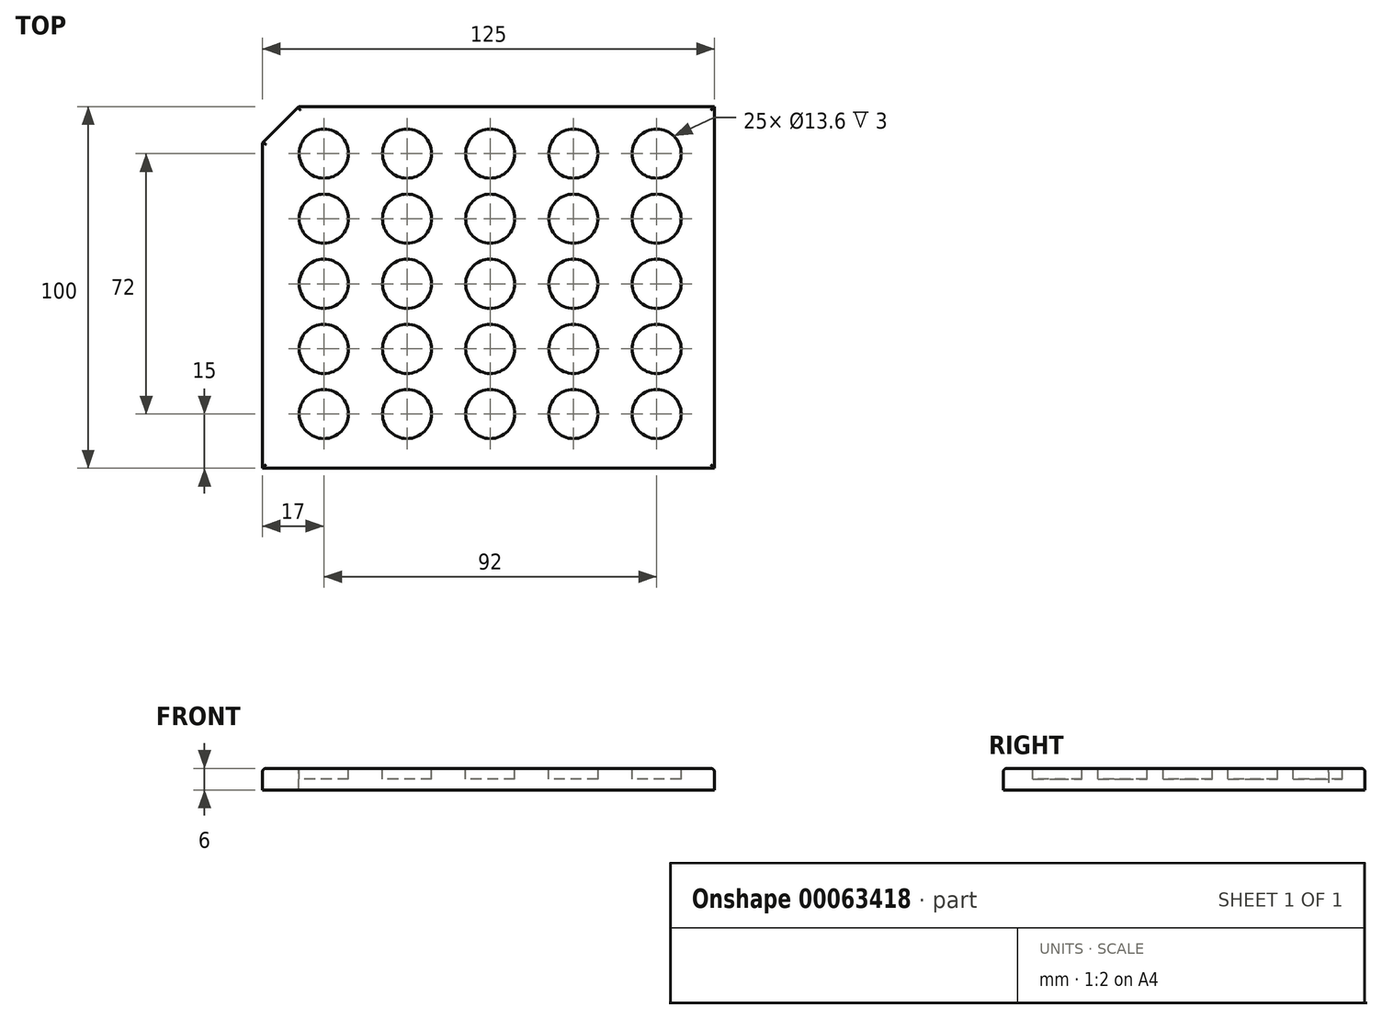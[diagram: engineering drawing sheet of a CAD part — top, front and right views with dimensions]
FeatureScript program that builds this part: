
annotation { "Feature Type Name" : "Feature", "Feature Type Description" : "" }
export const myFeature = defineFeature(function(context is Context, id is Id, definition is map)
    precondition{}
    {
        {
            var Q0;
            Q0=qCreatedBy(makeId("Top.planeOp"),FACE);
            var sketch = newSketch(context, id + "F0", { "sketchPlane" : qUnion([Q0])});
            skLineSegment(sketch, "E0.rect.bottom", {"start": v(62.5, -50) * mm, "end": v(-62.5, -50) * mm});
            skLineSegment(sketch, "E0.rect.top", {"start": v(62.5, 50) * mm, "end": v(-62.5, 50) * mm});
            skLineSegment(sketch, "E0.rect.left", {"start": v(62.5, -50) * mm, "end": v(62.5, 50) * mm});
            skLineSegment(sketch, "E0.rect.right", {"start": v(-62.5, -50) * mm, "end": v(-62.5, 50) * mm});
            skPoint(sketch, "E0.rect.middle", {"position": v(0, 0) * mm});
            skSolve(sketch);
        }
        {
            var Q0;
            Q0=qSketchRegion(id+"F0",true);
            extrude(context, id + "F1", {"entities" : qUnion([Q0]), "depth" : 6 * mm});
        }
        {
            var Q0;
            Q0=makeQuery(id+"F1.opExtrude","SWEPT_EDGE",EDGE,{"disambiguationData":[OSD([sQuery(id+"F0.wireOp",EDGE,"E0.rect.top"),sQuery(id+"F0.wireOp",EDGE,"E0.rect.right")])]});
            chamfer(context, id + "F2", {"entities" : qUnion([Q0]), "width" : 10 * mm, "tangentPropagation" : true});
        }
        {
            var Q0;
            Q0=makeQuery(id+"F1.opExtrude","CAP_EDGE",EDGE,{"disambiguationData":[OSD([sQuery(id+"F0.wireOp",EDGE,"E0.rect.right")])],"isStart":false});
            var Q1;
            Q1=makeQuery(id+"F1.opExtrude","CAP_EDGE",EDGE,{"disambiguationData":[OSD([sQuery(id+"F0.wireOp",EDGE,"E0.rect.bottom")])],"isStart":false});
            var Q2;
            Q2=makeQuery(id+"F1.opExtrude","CAP_EDGE",EDGE,{"disambiguationData":[OSD([sQuery(id+"F0.wireOp",EDGE,"E0.rect.left")])],"isStart":false});
            var Q3;
            Q3=makeQuery(id+"F1.opExtrude","CAP_EDGE",EDGE,{"disambiguationData":[OSD([sQuery(id+"F0.wireOp",EDGE,"E0.rect.top")])],"isStart":false});
            var Q4;
            {var subQ0=sQuery(id+"F0.wireOp",EDGE,"E0.rect.right");var subQ1=sQuery(id+"F0.wireOp",EDGE,"E0.rect.top");Q4=makeQuery(id+"F2.opChamfer","BLEND_EDGE",EDGE,{"blendedFrom":[makeQuery(id+"F1.opExtrude","SWEPT_EDGE",EDGE,{"disambiguationData":[OSD([subQ1,subQ0])]}),makeQuery(id+"F1.opExtrude","CAP_FACE",FACE,{"disambiguationData":[OSD([sQuery(id+"F0.wireOp",EDGE,"E0.rect.bottom"),subQ1,sQuery(id+"F0.wireOp",EDGE,"E0.rect.left"),subQ0])],"isStart":false})],"blendedInto":[makeQuery(id+"F1.opExtrude","CAP_FACE",FACE,{"disambiguationData":[OSD([sQuery(id+"F0.wireOp",EDGE,"E0.rect.bottom"),subQ1,sQuery(id+"F0.wireOp",EDGE,"E0.rect.left"),subQ0])],"isStart":false})]});}
            fillet(context, id + "F3", {"entities" : qUnion([Q0, Q1, Q2, Q3, Q4]), "radius" : 1 * mm, "tangentPropagation" : true, "allowEdgeOverflow" : false});
        }
        {
            var Q0;
            Q0=makeQuery(id+"F1.opExtrude","CAP_FACE",FACE,{"disambiguationData":[OSD([sQuery(id+"F0.wireOp",EDGE,"E0.rect.bottom"),sQuery(id+"F0.wireOp",EDGE,"E0.rect.top"),sQuery(id+"F0.wireOp",EDGE,"E0.rect.left"),sQuery(id+"F0.wireOp",EDGE,"E0.rect.right")])],"isStart":false});
            var sketch = newSketch(context, id + "F4", { "sketchPlane" : qUnion([Q0])});
            skCircle(sketch, "E1", {"center": v(46.5, 37) * mm, "radius": 6.8 * mm});
            skCircle(sketch, "E2.0.1.0", {"center": v(46.5, 19) * mm, "radius": 6.8 * mm});
            skCircle(sketch, "E2.1.0.0", {"center": v(23.5, 37) * mm, "radius": 6.8 * mm});
            skCircle(sketch, "E2.1.1.0", {"center": v(23.5, 19) * mm, "radius": 6.8 * mm});
            skCircle(sketch, "E2.2.0.0", {"center": v(0.5, 37) * mm, "radius": 6.8 * mm});
            skCircle(sketch, "E2.2.1.0", {"center": v(0.5, 19) * mm, "radius": 6.8 * mm});
            skLineSegment(sketch, "E2.direction1", {"start": v(46.5, 37) * mm, "end": v(23.5, 37) * mm, "construction": true});
            skLineSegment(sketch, "E2.direction2", {"start": v(46.5, 37) * mm, "end": v(46.5, 19) * mm, "construction": true});
            skCircle(sketch, "E3.0.0.2", {"center": v(46.5, 1) * mm, "radius": 6.8 * mm});
            skCircle(sketch, "E3.0.0.3", {"center": v(46.5, -17) * mm, "radius": 6.8 * mm});
            skCircle(sketch, "E3.0.1.2", {"center": v(23.5, 1) * mm, "radius": 6.8 * mm});
            skCircle(sketch, "E3.0.1.3", {"center": v(23.5, -17) * mm, "radius": 6.8 * mm});
            skCircle(sketch, "E3.0.2.2", {"center": v(0.5, 1) * mm, "radius": 6.8 * mm});
            skCircle(sketch, "E3.0.2.3", {"center": v(0.5, -17) * mm, "radius": 6.8 * mm});
            skCircle(sketch, "E4.0.3.0", {"center": v(-22.5, 37) * mm, "radius": 6.8 * mm});
            skCircle(sketch, "E4.0.3.1", {"center": v(-22.5, 19) * mm, "radius": 6.8 * mm});
            skCircle(sketch, "E4.0.3.2", {"center": v(-22.5, 1) * mm, "radius": 6.8 * mm});
            skCircle(sketch, "E4.0.3.3", {"center": v(-22.5, -17) * mm, "radius": 6.8 * mm});
            skCircle(sketch, "E4.0.4.0", {"center": v(-45.5, 37) * mm, "radius": 6.8 * mm});
            skCircle(sketch, "E4.0.4.1", {"center": v(-45.5, 19) * mm, "radius": 6.8 * mm});
            skCircle(sketch, "E4.0.4.2", {"center": v(-45.5, 1) * mm, "radius": 6.8 * mm});
            skCircle(sketch, "E4.0.4.3", {"center": v(-45.5, -17) * mm, "radius": 6.8 * mm});
            skCircle(sketch, "E5.0.0.4", {"center": v(46.5, -35) * mm, "radius": 6.8 * mm});
            skCircle(sketch, "E5.0.1.4", {"center": v(23.5, -35) * mm, "radius": 6.8 * mm});
            skCircle(sketch, "E5.0.2.4", {"center": v(0.5, -35) * mm, "radius": 6.8 * mm});
            skCircle(sketch, "E5.0.3.4", {"center": v(-22.5, -35) * mm, "radius": 6.8 * mm});
            skCircle(sketch, "E5.0.4.4", {"center": v(-45.5, -35) * mm, "radius": 6.8 * mm});
            skSolve(sketch);
        }
        {
            var Q0;
            Q0=qSketchRegion(id+"F4",true);
            extrude(context, id + "F5", {"entities" : qUnion([Q0]), "operationType" : NewBodyOperationType.REMOVE, "oppositeDirection" : true, "depth" : 3 * mm});
        }
    });
